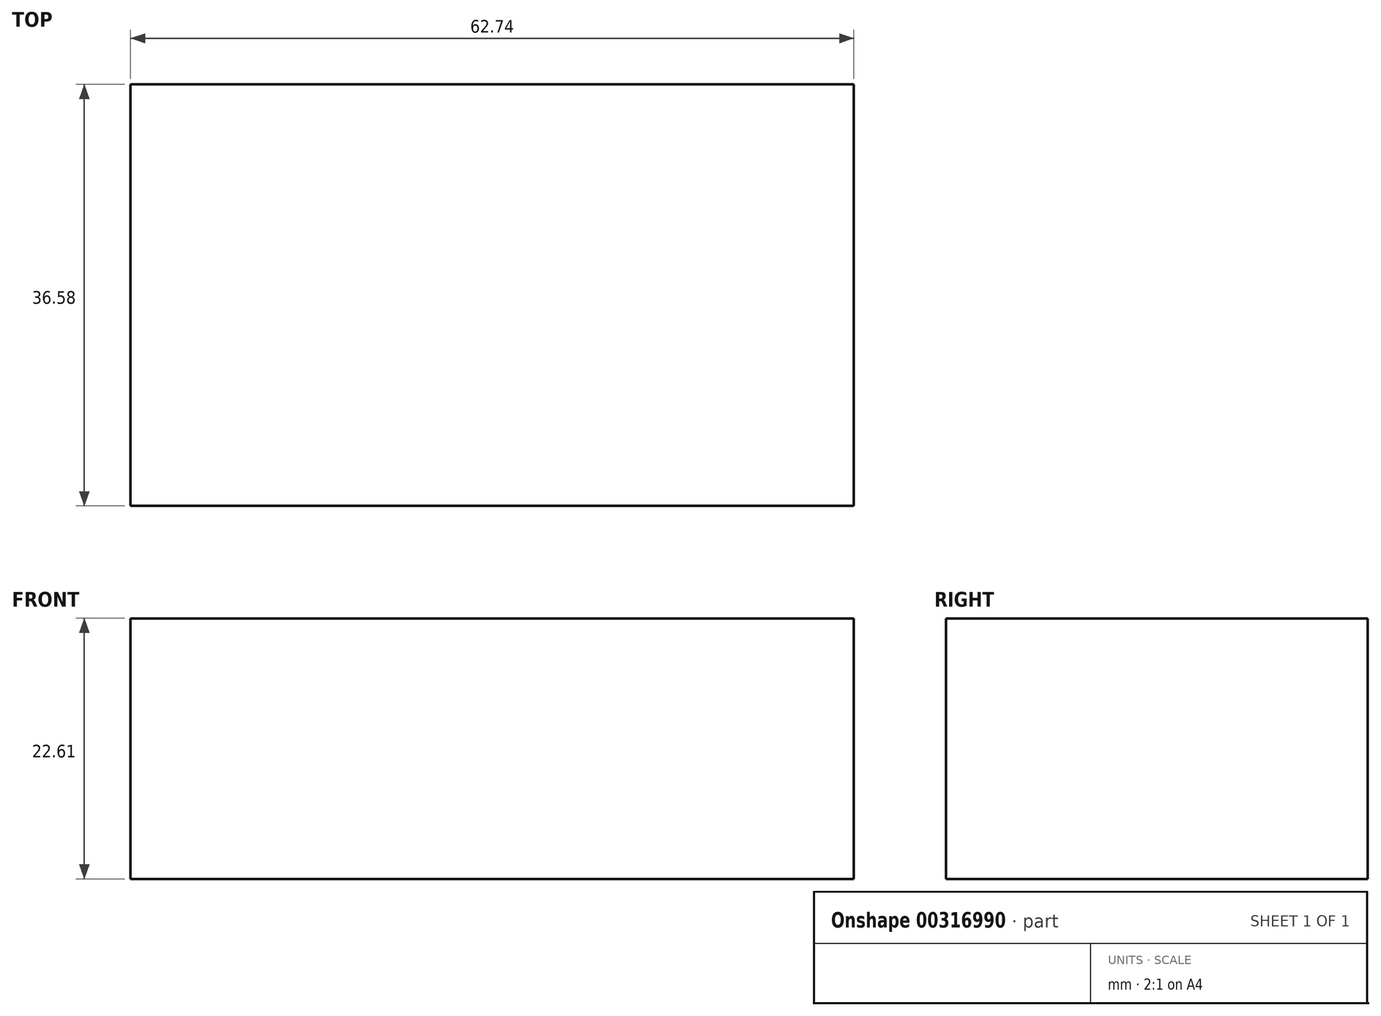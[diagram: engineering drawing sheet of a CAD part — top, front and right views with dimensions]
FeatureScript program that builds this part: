
annotation { "Feature Type Name" : "Feature", "Feature Type Description" : "" }
export const myFeature = defineFeature(function(context is Context, id is Id, definition is map)
    precondition{}
    {
        {
            var Q0;
            Q0=qCreatedBy(makeId("Front.planeOp"),FACE);
            var sketch = newSketch(context, id + "F0", { "sketchPlane" : qUnion([Q0])});
            skLineSegment(sketch, "E0.bottom", {"start": v(-51.58, 22.6) * mm, "end": v(11.16, 22.6) * mm});
            skLineSegment(sketch, "E0.top", {"start": v(-51.58, 0) * mm, "end": v(11.16, 0) * mm});
            skLineSegment(sketch, "E0.left", {"start": v(-51.58, 22.6) * mm, "end": v(-51.58, 0) * mm});
            skLineSegment(sketch, "E0.right", {"start": v(11.16, 22.6) * mm, "end": v(11.16, 0) * mm});
            skSolve(sketch);
        }
        {
            var Q0;
            Q0 = qSketchRegion(id + "F0", true);
            extrude(context, id + "F1", {"entities" : qUnion([Q0]), "depth" : 36.58 * mm});
        }
    });
